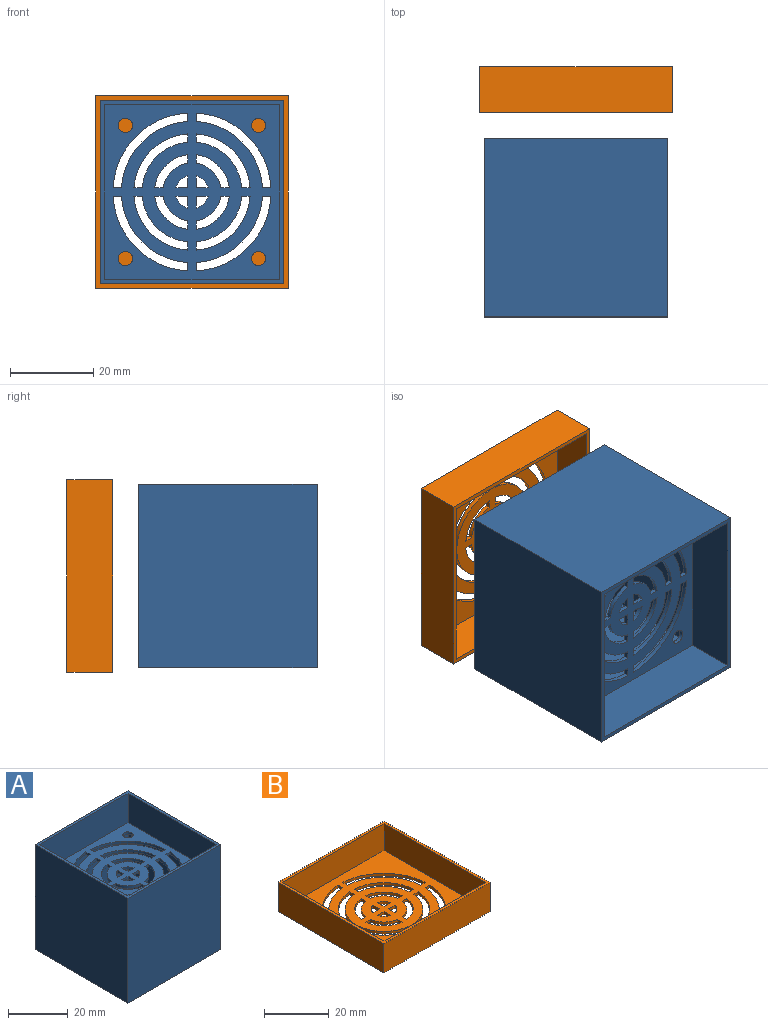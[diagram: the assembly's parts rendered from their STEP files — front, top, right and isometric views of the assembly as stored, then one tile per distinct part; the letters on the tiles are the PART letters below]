
ASSEMBLY  parts=2 mates=1
PART A: 80 faces, bbox 44x44x43 mm
  f0: plane 42x42mm, normal (0,0,1), area 1262.4mm2, adj f7,f8,f9,f10,f11,f12,f13,f14
  f1: plane 42x42mm, normal (0,0,-1), area 1262.4mm2, adj f11,f12,f13,f14,f15,f16,f17,f18
  f2: plane 44x44mm, normal (0,0,1), area 172mm2, adj f3,f4,f5,f6,f7,f8,f9,f10
  f3: plane 44x43mm, normal (1,0,0), area 1892mm2, adj f2,f4,f6,f75
  f4: plane 44x43mm, normal (0,1,0), area 1892mm2, adj f2,f3,f5,f75
  f5: plane 44x43mm, normal (-1,0,0), area 1892mm2, adj f2,f4,f6,f75
  f6: plane 44x43mm, normal (0,-1,0), area 1892mm2, adj f2,f3,f5,f75
  f7: plane 42x12mm, normal (-1,0,0), area 504mm2, adj f0,f2,f8,f10
  f8: plane 42x12mm, normal (0,-1,0), area 504mm2, adj f0,f2,f7,f9
  f9: plane 42x12mm, normal (1,0,0), area 504mm2, adj f0,f2,f8,f10
  f10: plane 42x12mm, normal (0,1,0), area 504mm2, adj f0,f2,f7,f9
  f11: plane 2x1mm, normal (-1,0,0), area 2mm2, adj f0,f1,f12,f14
  f12: cylinder r=19mm len=17.97mm, axis (0,0,1), area 27.8mm2, adj f0,f1,f11,f13
  f13: plane 2x1mm, normal (0,1,0), area 2mm2, adj f0,f1,f12,f14
  f14: cylinder r=17mm len=15.97mm, axis (0,0,1), area 24.7mm2, adj f0,f1,f11,f13
  f15: plane 2.01x1mm, normal (0,-1,0), area 2mm2, adj f0,f1,f16,f18
  f16: cylinder r=14mm len=12.96mm, axis (0,0,1), area 20mm2, adj f0,f1,f15,f17
  f17: plane 2.01x1mm, normal (-1,0,0), area 2mm2, adj f0,f1,f16,f18
  f18: cylinder r=12mm len=10.96mm, axis (0,0,1), area 16.8mm2, adj f0,f1,f15,f17
  f19: plane 2.02x1mm, normal (0,-1,0), area 2mm2, adj f0,f1,f20,f22
  f20: cylinder r=9mm len=7.94mm, axis (0,0,1), area 12.1mm2, adj f0,f1,f19,f21
  f21: plane 2.02x1mm, normal (-1,0,0), area 2mm2, adj f0,f1,f20,f22
  f22: cylinder r=7mm len=5.93mm, axis (0,0,1), area 9mm2, adj f0,f1,f19,f21
  f23: plane 2x1mm, normal (0,-1,0), area 2mm2, adj f0,f1,f24,f26
  f24: cylinder r=19mm len=17.97mm, axis (0,0,1), area 27.8mm2, adj f0,f1,f23,f25
  f25: plane 2x1mm, normal (-1,0,0), area 2mm2, adj f0,f1,f24,f26
  f26: cylinder r=17mm len=15.97mm, axis (0,0,1), area 24.7mm2, adj f0,f1,f23,f25
  f27: plane 2.02x1mm, normal (0,1,0), area 2mm2, adj f0,f1,f28,f30
  f28: cylinder r=7mm len=5.93mm, axis (0,0,1), area 9mm2, adj f0,f1,f27,f29
  f29: plane 2.02x1mm, normal (-1,0,0), area 2mm2, adj f0,f1,f28,f30
  f30: cylinder r=9mm len=7.94mm, axis (0,0,1), area 12.1mm2, adj f0,f1,f27,f29
  f31: plane 2.01x1mm, normal (-1,0,0), area 2mm2, adj f0,f1,f32,f34
  f32: cylinder r=14mm len=12.96mm, axis (0,0,1), area 20mm2, adj f0,f1,f31,f33
  f33: plane 2.01x1mm, normal (0,1,0), area 2mm2, adj f0,f1,f32,f34
  f34: cylinder r=12mm len=10.96mm, axis (0,0,1), area 16.8mm2, adj f0,f1,f31,f33
  f35: cylinder r=14mm len=12.96mm, axis (0,0,1), area 20mm2, adj f0,f1,f36,f38
  f36: plane 2.01x1mm, normal (1,0,0), area 2mm2, adj f0,f1,f35,f37
  f37: cylinder r=12mm len=10.96mm, axis (0,0,1), area 16.8mm2, adj f0,f1,f36,f38
  f38: plane 2.01x1mm, normal (0,1,0), area 2mm2, adj f0,f1,f35,f37
  f39: cylinder r=19mm len=17.97mm, axis (0,0,1), area 27.8mm2, adj f0,f1,f40,f42
  f40: plane 2x1mm, normal (1,0,0), area 2mm2, adj f0,f1,f39,f41
  f41: cylinder r=17mm len=15.97mm, axis (0,0,1), area 24.7mm2, adj f0,f1,f40,f42
  f42: plane 2x1mm, normal (0,1,0), area 2mm2, adj f0,f1,f39,f41
  f43: plane 2.01x1mm, normal (1,0,0), area 2mm2, adj f0,f1,f44,f46
  f44: cylinder r=14mm len=12.96mm, axis (0,0,1), area 20mm2, adj f0,f1,f43,f45
  f45: plane 2.01x1mm, normal (0,-1,0), area 2mm2, adj f0,f1,f44,f46
  f46: cylinder r=12mm len=10.96mm, axis (0,0,1), area 16.8mm2, adj f0,f1,f43,f45
  f47: cylinder r=17mm len=15.97mm, axis (0,0,1), area 24.7mm2, adj f0,f1,f48,f50
  f48: plane 2x1mm, normal (1,0,0), area 2mm2, adj f0,f1,f47,f49
  f49: cylinder r=19mm len=17.97mm, axis (0,0,1), area 27.8mm2, adj f0,f1,f48,f50
  f50: plane 2x1mm, normal (0,-1,0), area 2mm2, adj f0,f1,f47,f49
  f51: plane 2.02x1mm, normal (1,0,0), area 2mm2, adj f0,f1,f52,f54
  f52: cylinder r=9mm len=7.94mm, axis (0,0,1), area 12.1mm2, adj f0,f1,f51,f53
  f53: plane 2.02x1mm, normal (0,-1,0), area 2mm2, adj f0,f1,f52,f54
  f54: cylinder r=7mm len=5.93mm, axis (0,0,1), area 9mm2, adj f0,f1,f51,f53
  f55: cylinder r=7mm len=5.93mm, axis (0,0,1), area 9mm2, adj f0,f1,f56,f58
  f56: plane 2.02x1mm, normal (0,1,0), area 2mm2, adj f0,f1,f55,f57
  f57: cylinder r=9mm len=7.94mm, axis (0,0,1), area 12.1mm2, adj f0,f1,f56,f58
  f58: plane 2.02x1mm, normal (1,0,0), area 2mm2, adj f0,f1,f55,f57
  f59: cylinder r=4mm len=2.87mm, axis (0,0,1), area 4.3mm2, adj f0,f1,f60,f61
  f60: plane 2.87x1mm, normal (1,0,0), area 2.9mm2, adj f0,f1,f59,f61
  f61: plane 2.87x1mm, normal (0,1,0), area 2.9mm2, adj f0,f1,f59,f60
  f62: cylinder r=4mm len=2.87mm, axis (0,0,1), area 4.3mm2, adj f0,f1,f63,f64
  f63: plane 2.87x1mm, normal (0,1,0), area 2.9mm2, adj f0,f1,f62,f64
  f64: plane 2.87x1mm, normal (-1,0,0), area 2.9mm2, adj f0,f1,f62,f63
  f65: plane 2.87x1mm, normal (0,-1,0), area 2.9mm2, adj f0,f1,f66,f67
  f66: cylinder r=4mm len=2.87mm, axis (0,0,1), area 4.3mm2, adj f0,f1,f65,f67
  f67: plane 2.87x1mm, normal (-1,0,0), area 2.9mm2, adj f0,f1,f65,f66
  f68: plane 2.87x1mm, normal (0,-1,0), area 2.9mm2, adj f0,f1,f69,f70
  f69: plane 2.87x1mm, normal (1,0,0), area 2.9mm2, adj f0,f1,f68,f70
  f70: cylinder r=4mm len=2.87mm, axis (0,0,1), area 4.3mm2, adj f0,f1,f68,f69
  f71: plane 42x30mm, normal (0,1,0), area 1260mm2, adj f1,f72,f74,f75
  f72: plane 42x30mm, normal (-1,0,0), area 1260mm2, adj f1,f71,f73,f75
  f73: plane 42x30mm, normal (0,-1,0), area 1260mm2, adj f1,f72,f74,f75
  f74: plane 42x30mm, normal (1,0,0), area 1260mm2, adj f1,f71,f73,f75
  f75: plane 44x44mm, normal (0,0,-1), area 172mm2, adj f3,f4,f5,f6,f71,f72,f73,f74
  f76: cylinder r=1.71mm len=3.43mm, axis (0,0,1), area 10.8mm2, adj f0,f1
  f77: cylinder r=1.71mm len=3.43mm, axis (0,0,1), area 10.8mm2, adj f0,f1
  f78: cylinder r=1.71mm len=3.43mm, axis (0,0,1), area 10.8mm2, adj f0,f1
  f79: cylinder r=1.71mm len=3.43mm, axis (0,0,1), area 10.8mm2, adj f0,f1
PART B: 71 faces, bbox 46.2x46.2x11 mm
  f0: plane 44.2x44.2mm, normal (0,0,1), area 1489mm2, adj f2,f3,f4,f9,f11,f12,f13,f14
  f1: plane 46.2x46.2mm, normal (0,0,-1), area 1669.8mm2, adj f5,f6,f7,f8,f11,f12,f13,f14
  f2: plane 44.2x10mm, normal (1,0,0), area 442mm2, adj f0,f3,f9,f10
  f3: plane 44.2x10mm, normal (0,-1,0), area 442mm2, adj f0,f2,f4,f10
  f4: plane 44.2x10mm, normal (-1,0,0), area 442mm2, adj f0,f3,f9,f10
  f5: plane 46.2x11mm, normal (1,0,0), area 508.2mm2, adj f1,f6,f8,f10
  f6: plane 46.2x11mm, normal (0,1,0), area 508.2mm2, adj f1,f5,f7,f10
  f7: plane 46.2x11mm, normal (-1,0,0), area 508.2mm2, adj f1,f6,f8,f10
  f8: plane 46.2x11mm, normal (0,-1,0), area 508.2mm2, adj f1,f5,f7,f10
  f9: plane 44.2x10mm, normal (0,1,0), area 442mm2, adj f0,f2,f4,f10
  f10: plane 46.2x46.2mm, normal (0,0,1), area 180.8mm2, adj f2,f3,f4,f5,f6,f7,f8,f9
  f11: cylinder r=19mm len=17.97mm, axis (0,0,1), area 27.8mm2, adj f0,f1,f12,f14
  f12: plane 2x1mm, normal (1,0,0), area 2mm2, adj f0,f1,f11,f13
  f13: cylinder r=17mm len=15.97mm, axis (0,0,1), area 24.7mm2, adj f0,f1,f12,f14
  f14: plane 2x1mm, normal (0,1,0), area 2mm2, adj f0,f1,f11,f13
  f15: plane 2.01x1mm, normal (1,0,0), area 2mm2, adj f0,f1,f16,f18
  f16: cylinder r=14mm len=12.96mm, axis (0,0,1), area 20mm2, adj f0,f1,f15,f17
  f17: plane 2.01x1mm, normal (0,-1,0), area 2mm2, adj f0,f1,f16,f18
  f18: cylinder r=12mm len=10.96mm, axis (0,0,1), area 16.8mm2, adj f0,f1,f15,f17
  f19: cylinder r=17mm len=15.97mm, axis (0,0,1), area 24.7mm2, adj f0,f1,f20,f22
  f20: plane 2x1mm, normal (1,0,0), area 2mm2, adj f0,f1,f19,f21
  f21: cylinder r=19mm len=17.97mm, axis (0,0,1), area 27.8mm2, adj f0,f1,f20,f22
  f22: plane 2x1mm, normal (0,-1,0), area 2mm2, adj f0,f1,f19,f21
  f23: plane 2.02x1mm, normal (1,0,0), area 2mm2, adj f0,f1,f24,f26
  f24: cylinder r=9mm len=7.94mm, axis (0,0,1), area 12.1mm2, adj f0,f1,f23,f25
  f25: plane 2.02x1mm, normal (0,-1,0), area 2mm2, adj f0,f1,f24,f26
  f26: cylinder r=7mm len=5.93mm, axis (0,0,1), area 9mm2, adj f0,f1,f23,f25
  f27: plane 2.02x1mm, normal (0,-1,0), area 2mm2, adj f0,f1,f28,f30
  f28: cylinder r=9mm len=7.94mm, axis (0,0,1), area 12.1mm2, adj f0,f1,f27,f29
  f29: plane 2.02x1mm, normal (-1,0,0), area 2mm2, adj f0,f1,f28,f30
  f30: cylinder r=7mm len=5.93mm, axis (0,0,1), area 9mm2, adj f0,f1,f27,f29
  f31: plane 2.87x1mm, normal (0,-1,0), area 2.9mm2, adj f0,f1,f32,f33
  f32: cylinder r=4mm len=2.87mm, axis (0,0,1), area 4.3mm2, adj f0,f1,f31,f33
  f33: plane 2.87x1mm, normal (-1,0,0), area 2.9mm2, adj f0,f1,f31,f32
  f34: plane 2x1mm, normal (0,-1,0), area 2mm2, adj f0,f1,f35,f37
  f35: cylinder r=19mm len=17.97mm, axis (0,0,1), area 27.8mm2, adj f0,f1,f34,f36
  f36: plane 2x1mm, normal (-1,0,0), area 2mm2, adj f0,f1,f35,f37
  f37: cylinder r=17mm len=15.97mm, axis (0,0,1), area 24.7mm2, adj f0,f1,f34,f36
  f38: plane 2.01x1mm, normal (0,-1,0), area 2mm2, adj f0,f1,f39,f41
  f39: cylinder r=14mm len=12.96mm, axis (0,0,1), area 20mm2, adj f0,f1,f38,f40
  f40: plane 2.01x1mm, normal (-1,0,0), area 2mm2, adj f0,f1,f39,f41
  f41: cylinder r=12mm len=10.96mm, axis (0,0,1), area 16.8mm2, adj f0,f1,f38,f40
  f42: plane 2.01x1mm, normal (-1,0,0), area 2mm2, adj f0,f1,f43,f45
  f43: cylinder r=14mm len=12.96mm, axis (0,0,1), area 20mm2, adj f0,f1,f42,f44
  f44: plane 2.01x1mm, normal (0,1,0), area 2mm2, adj f0,f1,f43,f45
  f45: cylinder r=12mm len=10.96mm, axis (0,0,1), area 16.8mm2, adj f0,f1,f42,f44
  f46: plane 2x1mm, normal (-1,0,0), area 2mm2, adj f0,f1,f47,f49
  f47: cylinder r=19mm len=17.97mm, axis (0,0,1), area 27.8mm2, adj f0,f1,f46,f48
  f48: plane 2x1mm, normal (0,1,0), area 2mm2, adj f0,f1,f47,f49
  f49: cylinder r=17mm len=15.97mm, axis (0,0,1), area 24.7mm2, adj f0,f1,f46,f48
  f50: cylinder r=7mm len=5.93mm, axis (0,0,1), area 9mm2, adj f0,f1,f51,f53
  f51: plane 2.02x1mm, normal (0,1,0), area 2mm2, adj f0,f1,f50,f52
  f52: cylinder r=9mm len=7.94mm, axis (0,0,1), area 12.1mm2, adj f0,f1,f51,f53
  f53: plane 2.02x1mm, normal (1,0,0), area 2mm2, adj f0,f1,f50,f52
  f54: cylinder r=14mm len=12.96mm, axis (0,0,1), area 20mm2, adj f0,f1,f55,f57
  f55: plane 2.01x1mm, normal (1,0,0), area 2mm2, adj f0,f1,f54,f56
  f56: cylinder r=12mm len=10.96mm, axis (0,0,1), area 16.8mm2, adj f0,f1,f55,f57
  f57: plane 2.01x1mm, normal (0,1,0), area 2mm2, adj f0,f1,f54,f56
  f58: cylinder r=4mm len=2.87mm, axis (0,0,1), area 4.3mm2, adj f0,f1,f59,f60
  f59: plane 2.87x1mm, normal (0,1,0), area 2.9mm2, adj f0,f1,f58,f60
  f60: plane 2.87x1mm, normal (-1,0,0), area 2.9mm2, adj f0,f1,f58,f59
  f61: plane 2.02x1mm, normal (0,1,0), area 2mm2, adj f0,f1,f62,f64
  f62: cylinder r=7mm len=5.93mm, axis (0,0,1), area 9mm2, adj f0,f1,f61,f63
  f63: plane 2.02x1mm, normal (-1,0,0), area 2mm2, adj f0,f1,f62,f64
  f64: cylinder r=9mm len=7.94mm, axis (0,0,1), area 12.1mm2, adj f0,f1,f61,f63
  f65: cylinder r=4mm len=2.87mm, axis (0,0,1), area 4.3mm2, adj f0,f1,f66,f67
  f66: plane 2.87x1mm, normal (1,0,0), area 2.9mm2, adj f0,f1,f65,f67
  f67: plane 2.87x1mm, normal (0,1,0), area 2.9mm2, adj f0,f1,f65,f66
  f68: plane 2.87x1mm, normal (0,-1,0), area 2.9mm2, adj f0,f1,f69,f70
  f69: plane 2.87x1mm, normal (1,0,0), area 2.9mm2, adj f0,f1,f68,f70
  f70: cylinder r=4mm len=2.87mm, axis (0,0,1), area 4.3mm2, adj f0,f1,f68,f69
PLACE A rot(axis=(1,0,0),90deg) t=(-40.02,-95.06,-20.91)mm
PLACE B rot(axis=(1,0,0),90deg) t=(-40.02,-47.92,-20.91)mm
MATE slider A.f70 <-> B.f37  axis (0,-1,0) through (-40.02,-96.06,-20.91)mm
